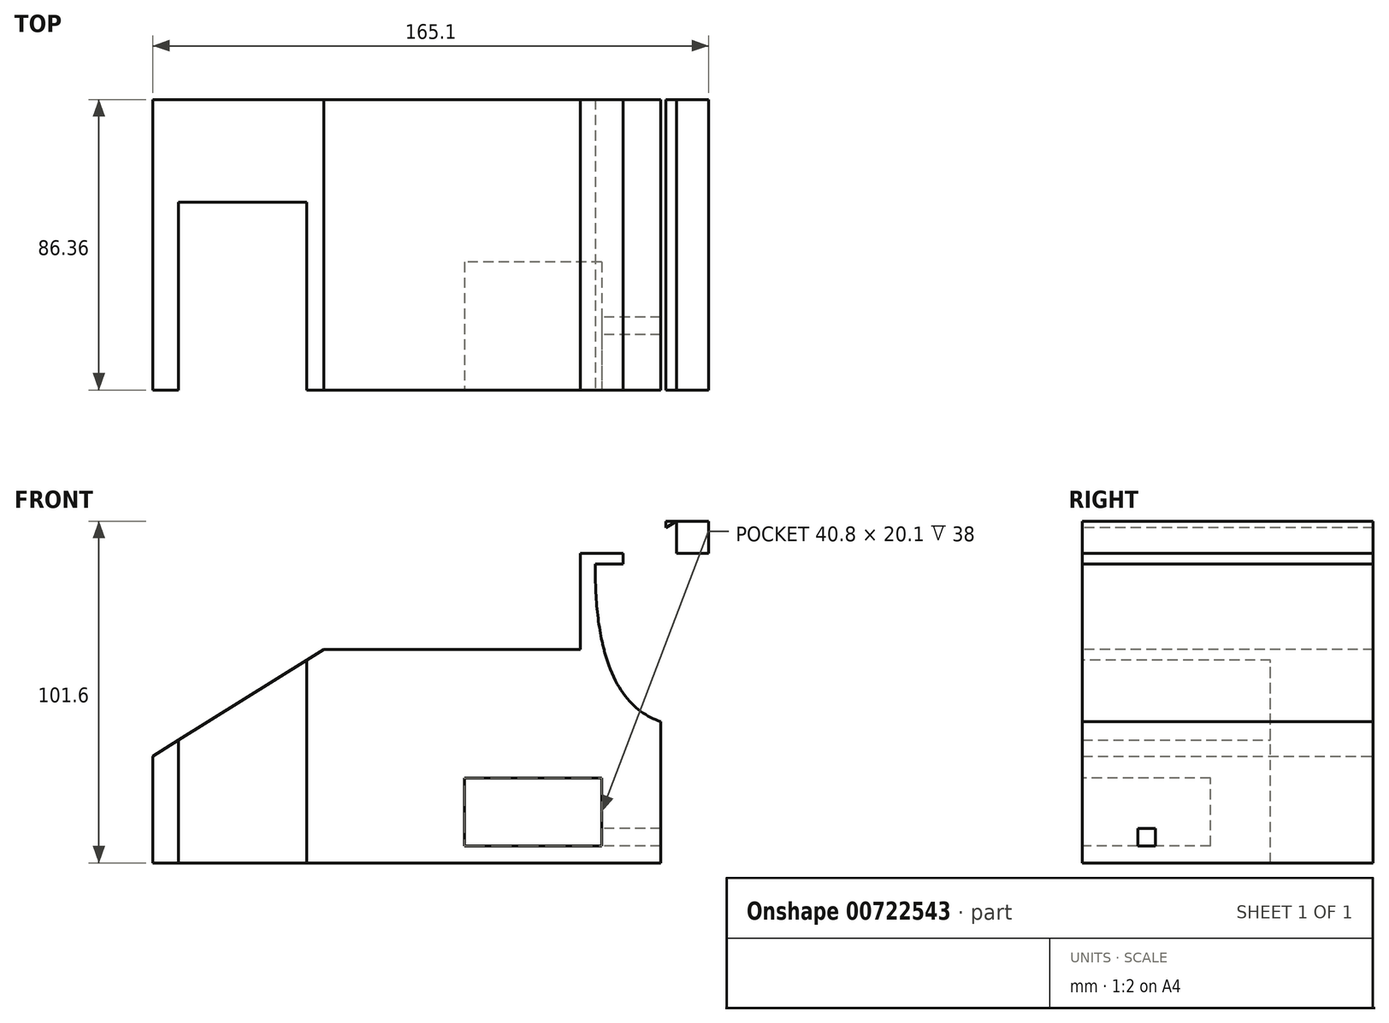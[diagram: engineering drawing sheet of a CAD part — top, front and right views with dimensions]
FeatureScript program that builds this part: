
annotation { "Feature Type Name" : "Feature", "Feature Type Description" : "" }
export const myFeature = defineFeature(function(context is Context, id is Id, definition is map)
    precondition{}
    {
        {
            var Q0;
            Q0=qCreatedBy(makeId("Top.planeOp"),FACE);
            var sketch = newSketch(context, id + "F0", { "sketchPlane" : qUnion([Q0])});
            skLineSegment(sketch, "E0.bottom", {"start": v(25.4, -38.7) * mm, "end": v(-25.4, -38.7) * mm});
            skLineSegment(sketch, "E0.top", {"start": v(25.4, 47.66) * mm, "end": v(-25.4, 47.66) * mm});
            skLineSegment(sketch, "E0.left", {"start": v(25.4, -38.7) * mm, "end": v(25.4, 47.66) * mm});
            skLineSegment(sketch, "E0.right", {"start": v(-25.4, -38.7) * mm, "end": v(-25.4, 47.66) * mm});
            skPoint(sketch, "E0.middle", {"position": v(0, 4.48) * mm});
            skSolve(sketch);
        }
        {
            var Q0;
            Q0=makeQuery(id+"F0.imprint","IMPRINT",FACE,{"disambiguationData":[TD([[makeQuery(id+"F0.imprint","IMPRINT",EDGE,{"derivedFrom":sQuery(id+"F0.wireOp",EDGE,"E0.bottom")}),-1.0]])]});
            extrude(context, id + "F1", {"entities" : qUnion([Q0]), "depth" : 63.5 * mm, "offsetDistance" : 25.4 * mm});
        }
        {
            var Q0;
            Q0=makeQuery(id+"F1.opExtrude","CAP_FACE",FACE,{"disambiguationData":[OSD([sQuery(id+"F0.wireOp",EDGE,"E0.bottom"),sQuery(id+"F0.wireOp",EDGE,"E0.top"),sQuery(id+"F0.wireOp",EDGE,"E0.left"),sQuery(id+"F0.wireOp",EDGE,"E0.right")])],"isStart":false});
            var sketch = newSketch(context, id + "F2", { "sketchPlane" : qUnion([Q0])});
            skLineSegment(sketch, "E1", {"start": v(0, 47.66) * mm, "end": v(0, -38.7) * mm});
            skLineSegment(sketch, "E2", {"start": v(-25.4, 4.48) * mm, "end": v(25.4, 4.48) * mm});
            skPoint(sketch, "E3.middle", {"position": v(0, 4.48) * mm});
            skLineSegment(sketch, "E4", {"start": v(-25.4, -38.7) * mm, "end": v(-17.78, -38.7) * mm});
            skLineSegment(sketch, "E5", {"start": v(25.4, -38.7) * mm, "end": v(20.32, -38.7) * mm});
            skLineSegment(sketch, "E6", {"start": v(20.32, -38.7) * mm, "end": v(20.32, 17.18) * mm});
            skLineSegment(sketch, "E7", {"start": v(20.32, 17.18) * mm, "end": v(-17.78, 17.18) * mm});
            skLineSegment(sketch, "E8", {"start": v(-17.78, 17.18) * mm, "end": v(-17.78, -38.7) * mm});
            skSolve(sketch);
        }
        {
            var Q0;
            {var subQ0=sQuery(id+"F2.wireOp",EDGE,"E1");var subQ1=makeQuery(id+"F1.opExtrude","CAP_EDGE",EDGE,{"disambiguationData":[OSD([sQuery(id+"F0.wireOp",EDGE,"E0.bottom")])],"isStart":false});var subQ2=makeQuery(id+"F2.imprint","INTERSECT",VERTEX,{"derivedFrom":[subQ1,subQ0]});Q0=makeQuery(id+"F2.imprint","IMPRINT",FACE,{"disambiguationData":[TD([[makeQuery(id+"F2.imprint","IMPRINT",EDGE,{"disambiguationData":[TD([[subQ2,1.0]])],"derivedFrom":subQ0}),1.0]])]});}
            var Q1;
            {var subQ0=sQuery(id+"F2.wireOp",EDGE,"E1");var subQ1=makeQuery(id+"F1.opExtrude","CAP_EDGE",EDGE,{"disambiguationData":[OSD([sQuery(id+"F0.wireOp",EDGE,"E0.bottom")])],"isStart":false});var subQ2=makeQuery(id+"F2.imprint","INTERSECT",VERTEX,{"derivedFrom":[subQ1,subQ0]});Q1=makeQuery(id+"F2.imprint","IMPRINT",FACE,{"disambiguationData":[TD([[makeQuery(id+"F2.imprint","IMPRINT",EDGE,{"disambiguationData":[TD([[subQ2,1.0]])],"derivedFrom":subQ0}),-1.0]])]});}
            var Q2;
            {var subQ0=sQuery(id+"F2.wireOp",EDGE,"E7");var subQ1=sQuery(id+"F2.wireOp",EDGE,"E1");var subQ2=makeQuery(id+"F2.imprint","INTERSECT",VERTEX,{"derivedFrom":[subQ1,subQ0]});Q2=makeQuery(id+"F2.imprint","IMPRINT",FACE,{"disambiguationData":[TD([[makeQuery(id+"F2.imprint","IMPRINT",EDGE,{"disambiguationData":[TD([[subQ2,-1.0]])],"derivedFrom":subQ1}),-1.0]])]});}
            var Q3;
            {var subQ0=sQuery(id+"F2.wireOp",EDGE,"E7");var subQ1=sQuery(id+"F2.wireOp",EDGE,"E1");var subQ2=makeQuery(id+"F2.imprint","INTERSECT",VERTEX,{"derivedFrom":[subQ1,subQ0]});Q3=makeQuery(id+"F2.imprint","IMPRINT",FACE,{"disambiguationData":[TD([[makeQuery(id+"F2.imprint","IMPRINT",EDGE,{"disambiguationData":[TD([[subQ2,-1.0]])],"derivedFrom":subQ1}),1.0]])]});}
            extrude(context, id + "F3", {"entities" : qUnion([Q0, Q1, Q2, Q3]), "operationType" : NewBodyOperationType.REMOVE, "oppositeDirection" : true, "depth" : 228.6 * mm, "offsetDistance" : 25.4 * mm});
        }
        {
            var Q0;
            Q0=makeQuery(id+"F1.opExtrude","SWEPT_FACE",FACE,{"disambiguationData":[OSD([sQuery(id+"F0.wireOp",EDGE,"E0.top")])]});
            var sketch = newSketch(context, id + "F4", { "sketchPlane" : qUnion([Q0])});
            skLineSegment(sketch, "E9", {"start": v(25.4, 0) * mm, "end": v(25.4, 31.75) * mm});
            skLineSegment(sketch, "E10", {"start": v(25.4, 31.75) * mm, "end": v(-25.4, 63.5) * mm});
            skSolve(sketch);
        }
        {
            var Q0;
            {var subQ0=sQuery(id+"F4.wireOp",EDGE,"E10");Q0=makeQuery(id+"F4.imprint","IMPRINT",FACE,{"disambiguationData":[TD([[makeQuery(id+"F4.imprint","IMPRINT",EDGE,{"derivedFrom":subQ0}),-1.0]])]});}
            extrude(context, id + "F5", {"entities" : qUnion([Q0]), "operationType" : NewBodyOperationType.REMOVE, "oppositeDirection" : true, "depth" : 228.6 * mm, "offsetDistance" : 25.4 * mm});
        }
        {
            var Q0;
            Q0=makeQuery(id+"F1.opExtrude","SWEPT_FACE",FACE,{"disambiguationData":[OSD([sQuery(id+"F0.wireOp",EDGE,"E0.left")])]});
            var sketch = newSketch(context, id + "F6", { "sketchPlane" : qUnion([Q0])});
            skLineSegment(sketch, "E11.bottom", {"start": v(-38.7, 0) * mm, "end": v(47.66, 0) * mm});
            skLineSegment(sketch, "E11.top", {"start": v(-38.7, 114.3) * mm, "end": v(47.66, 114.3) * mm});
            skLineSegment(sketch, "E11.left", {"start": v(-38.7, 0) * mm, "end": v(-38.7, 114.3) * mm});
            skLineSegment(sketch, "E11.right", {"start": v(47.66, 0) * mm, "end": v(47.66, 114.3) * mm});
            skSolve(sketch);
        }
        {
            var Q0;
            {var subQ0=sQuery(id+"F6.wireOp",EDGE,"E11.top");Q0=makeQuery(id+"F6.imprint","IMPRINT",FACE,{"disambiguationData":[TD([[makeQuery(id+"F6.imprint","IMPRINT",EDGE,{"derivedFrom":subQ0}),-1.0]])]});}
            var Q1;
            {var subQ0=sQuery(id+"F6.wireOp",EDGE,"E11.bottom");Q1=makeQuery(id+"F6.imprint","IMPRINT",FACE,{"disambiguationData":[TD([[makeQuery(id+"F6.imprint","IMPRINT",EDGE,{"derivedFrom":subQ0}),1.0]])]});}
            extrude(context, id + "F7", {"entities" : qUnion([Q0, Q1]), "operationType" : NewBodyOperationType.ADD, "depth" : 127 * mm, "offsetDistance" : 25.4 * mm});
        }
        {
            var Q0;
            {var subQ1=sQuery(id+"F0.wireOp",EDGE,"E0.left");var subQ3=sQuery(id+"F0.wireOp",EDGE,"E0.bottom");Q0=makeQuery(id+"F7.boolean.opBoolean","MERGE",FACE,{"derivedFrom":[makeQuery(id+"F3.boolean.opBoolean","SPLIT",FACE,{"disambiguationData":[TD([makeQuery(id+"F1.opExtrude","SWEPT_FACE",FACE,{"disambiguationData":[OSD([subQ1])]})])],"derivedFrom":makeQuery(id+"F1.opExtrude","SWEPT_FACE",FACE,{"disambiguationData":[OSD([subQ3])]})}),makeQuery(id+"F7.opExtrude","SWEPT_FACE",FACE,{"disambiguationData":[OSD([sQuery(id+"F6.wireOp",EDGE,"E11.left")])]})]});}
            var sketch = newSketch(context, id + "F8", { "sketchPlane" : qUnion([Q0])});
            skLineSegment(sketch, "E12", {"start": v(25.4, 63.5) * mm, "end": v(152.4, 63.5) * mm});
            skLineSegment(sketch, "E13", {"start": v(152.4, 114.3) * mm, "end": v(101.6, 114.3) * mm});
            skLineSegment(sketch, "E14", {"start": v(101.6, 114.3) * mm, "end": v(101.6, 63.5) * mm});
            skLineSegment(sketch, "E15", {"start": v(101.6, 63.5) * mm, "end": v(101.6, 88.9) * mm});
            skFitSpline(sketch, "E16", {"points": [v(101.6, 88.9) * mm, v(56.46, 63.5) * mm, v(25.4, 114.3) * mm, v(19.9, 130.64) * mm], "startDerivative": vector(-196.62, -34.97) * mm, "endDerivative": vector(-5.13, 63.21) * mm});
            skSolve(sketch);
        }
        {
            var Q0;
            {var subQ1=sQuery(id+"F0.wireOp",EDGE,"E0.left");var subQ3=sQuery(id+"F0.wireOp",EDGE,"E0.bottom");Q0=makeQuery(id+"F7.boolean.opBoolean","MERGE",FACE,{"derivedFrom":[makeQuery(id+"F3.boolean.opBoolean","SPLIT",FACE,{"disambiguationData":[TD([makeQuery(id+"F1.opExtrude","SWEPT_FACE",FACE,{"disambiguationData":[OSD([subQ1])]})])],"derivedFrom":makeQuery(id+"F1.opExtrude","SWEPT_FACE",FACE,{"disambiguationData":[OSD([subQ3])]})}),makeQuery(id+"F7.opExtrude","SWEPT_FACE",FACE,{"disambiguationData":[OSD([sQuery(id+"F6.wireOp",EDGE,"E11.left")])]})]});}
            var sketch = newSketch(context, id + "F9", { "sketchPlane" : qUnion([Q0])});
            skLineSegment(sketch, "E17", {"start": v(25.4, 63.5) * mm, "end": v(152.4, 63.5) * mm});
            skSolve(sketch);
        }
        {
            var Q0;
            Q0=qSketchRegion(id+"F9",true);
            var Q1;
            {var subQ1=sQuery(id+"F6.wireOp",EDGE,"E11.left");var subQ2=makeQuery(id+"F7.opExtrude","CAP_EDGE",EDGE,{"disambiguationData":[OSD([subQ1])],"isStart":true});Q1=makeQuery(id+"F9.imprint","IMPRINT",FACE,{"disambiguationData":[TD([[makeQuery(id+"F9.imprint","IMPRINT",EDGE,{"derivedFrom":subQ2}),-1.0]])]});}
            extrude(context, id + "F10", {"entities" : qUnion([Q0, Q1]), "operationType" : NewBodyOperationType.REMOVE, "oppositeDirection" : true, "depth" : 228.6 * mm, "offsetDistance" : 25.4 * mm});
        }
        {
            var Q0;
            {var subQ1=sQuery(id+"F0.wireOp",EDGE,"E0.left");var subQ3=sQuery(id+"F0.wireOp",EDGE,"E0.bottom");Q0=makeQuery(id+"F7.boolean.opBoolean","MERGE",FACE,{"derivedFrom":[makeQuery(id+"F3.boolean.opBoolean","SPLIT",FACE,{"disambiguationData":[TD([makeQuery(id+"F1.opExtrude","SWEPT_FACE",FACE,{"disambiguationData":[OSD([subQ1])]})])],"derivedFrom":makeQuery(id+"F1.opExtrude","SWEPT_FACE",FACE,{"disambiguationData":[OSD([subQ3])]})}),makeQuery(id+"F7.opExtrude","SWEPT_FACE",FACE,{"disambiguationData":[OSD([sQuery(id+"F6.wireOp",EDGE,"E11.left")])]})]});}
            var sketch = newSketch(context, id + "F11", { "sketchPlane" : qUnion([Q0])});
            skLineSegment(sketch, "E18", {"start": v(152.4, 13.36) * mm, "end": v(107.95, 13.36) * mm});
            skLineSegment(sketch, "E19", {"start": v(107.95, 5.08) * mm, "end": v(107.95, 13.36) * mm});
            skLineSegment(sketch, "E20", {"start": v(107.95, 5.08) * mm, "end": v(67.15, 5.08) * mm});
            skLineSegment(sketch, "E21", {"start": v(67.15, 5.08) * mm, "end": v(67.15, 25.18) * mm});
            skLineSegment(sketch, "E22", {"start": v(67.15, 25.18) * mm, "end": v(107.95, 25.18) * mm});
            skLineSegment(sketch, "E23", {"start": v(107.95, 25.18) * mm, "end": v(107.95, 5.08) * mm});
            skSolve(sketch);
        }
        {
            var Q0;
            {var subQ1=sQuery(id+"F11.wireOp",EDGE,"E21");Q0=makeQuery(id+"F11.imprint","IMPRINT",FACE,{"disambiguationData":[TD([[makeQuery(id+"F11.imprint","IMPRINT",EDGE,{"derivedFrom":subQ1}),-1.0]])]});}
            extrude(context, id + "F12", {"entities" : qUnion([Q0]), "operationType" : NewBodyOperationType.REMOVE, "oppositeDirection" : true, "depth" : 38 * mm, "offsetDistance" : 25.4 * mm});
        }
        {
            var Q0;
            {var subQ0=sQuery(id+"F8.wireOp",EDGE,"E15");Q0=makeQuery(id+"F8.imprint","IMPRINT",FACE,{"disambiguationData":[TD([[makeQuery(id+"F8.imprint","IMPRINT",EDGE,{"derivedFrom":subQ0}),1.0]])]});}
            var Q1;
            {var subQ1=sQuery(id+"F8.wireOp",EDGE,"E13");Q1=makeQuery(id+"F8.imprint","IMPRINT",FACE,{"disambiguationData":[TD([[makeQuery(id+"F8.imprint","IMPRINT",EDGE,{"derivedFrom":subQ1}),1.0]])]});}
            extrude(context, id + "F13", {"entities" : qUnion([Q0, Q1]), "operationType" : NewBodyOperationType.ADD, "oppositeDirection" : true, "depth" : 86.36 * mm, "offsetDistance" : 25.4 * mm});
        }
        {
            var Q0;
            {var subQ0=sQuery(id+"F6.wireOp",EDGE,"E11.left");Q0=makeQuery(id+"F13.boolean.opBoolean","MERGE",FACE,{"derivedFrom":[makeQuery(id+"F7.opExtrude","CAP_FACE",FACE,{"disambiguationData":[OSD([sQuery(id+"F6.wireOp",EDGE,"E11.bottom"),sQuery(id+"F6.wireOp",EDGE,"E11.top"),subQ0,sQuery(id+"F6.wireOp",EDGE,"E11.right")])],"isStart":false}),makeQuery(id+"F13.opExtrude","SWEPT_FACE",FACE,{"disambiguationData":[OSD([subQ0])]})]});}
            var sketch = newSketch(context, id + "F14", { "sketchPlane" : qUnion([Q0])});
            skLineSegment(sketch, "E24", {"start": v(-38.7, 114.3) * mm, "end": v(-38.7, 88.9) * mm});
            skLineSegment(sketch, "E25", {"start": v(-38.7, 88.9) * mm, "end": v(47.66, 88.9) * mm});
            skLineSegment(sketch, "E26", {"start": v(47.66, 88.9) * mm, "end": v(47.66, 101.6) * mm});
            skSolve(sketch);
        }
        {
            var Q0;
            Q0=makeQuery(id+"F14.imprint","IMPRINT",FACE,{"disambiguationData":[TD([[makeQuery(id+"F14.imprint","IMPRINT",EDGE,{"derivedFrom":sQuery(id+"F14.wireOp",EDGE,"E24")}),-1.0]])]});
            extrude(context, id + "F15", {"entities" : qUnion([Q0]), "operationType" : NewBodyOperationType.REMOVE, "oppositeDirection" : true, "depth" : 101.6 * mm, "offsetDistance" : 25.4 * mm});
        }
        {
            var Q0;
            {var subQ0=sQuery(id+"F6.wireOp",EDGE,"E11.left");var subQ2=sQuery(id+"F0.wireOp",EDGE,"E0.left");var subQ4=sQuery(id+"F0.wireOp",EDGE,"E0.bottom");Q0=makeQuery(id+"F13.boolean.opBoolean","MERGE",FACE,{"derivedFrom":[makeQuery(id+"F7.boolean.opBoolean","MERGE",FACE,{"derivedFrom":[makeQuery(id+"F3.boolean.opBoolean","SPLIT",FACE,{"disambiguationData":[TD([makeQuery(id+"F1.opExtrude","SWEPT_FACE",FACE,{"disambiguationData":[OSD([subQ2])]})])],"derivedFrom":makeQuery(id+"F1.opExtrude","SWEPT_FACE",FACE,{"disambiguationData":[OSD([subQ4])]})}),makeQuery(id+"F7.opExtrude","SWEPT_FACE",FACE,{"disambiguationData":[OSD([subQ0])]})]}),makeQuery(id+"F13.opExtrude","CAP_FACE",FACE,{"disambiguationData":[OSD([subQ0,sQuery(id+"F8.wireOp",EDGE,"E12"),sQuery(id+"F8.wireOp",EDGE,"E13"),sQuery(id+"F8.wireOp",EDGE,"E14"),sQuery(id+"F8.wireOp",EDGE,"E16")])],"isStart":true})]});}
            var sketch = newSketch(context, id + "F16", { "sketchPlane" : qUnion([Q0])});
            skLineSegment(sketch, "E27", {"start": v(101.6, 88.9) * mm, "end": v(101.6, 0) * mm});
            skLineSegment(sketch, "E28", {"start": v(101.6, 0) * mm, "end": v(101.6, 44.45) * mm});
            skLineSegment(sketch, "E29", {"start": v(101.6, 44.45) * mm, "end": v(101.6, 88.9) * mm});
            skLineSegment(sketch, "E30", {"start": v(101.6, 66.68) * mm, "end": v(152.4, 66.68) * mm});
            skLineSegment(sketch, "E31", {"start": v(101.6, 88.9) * mm, "end": v(110.49, 88.9) * mm});
            skLineSegment(sketch, "E32", {"start": v(110.49, 88.9) * mm, "end": v(110.49, 0) * mm});
            skLineSegment(sketch, "E33", {"start": v(125.47, 45.06) * mm, "end": v(125.47, 0) * mm});
            skFitSpline(sketch, "E34", {"points": [v(106.04, 88.9) * mm, v(152.4, 44.45) * mm, v(157.72, 45.76) * mm], "startDerivative": vector(-2.32, -246.99) * mm, "endDerivative": vector(30.68, 18.7) * mm});
            skSolve(sketch);
        }
        {
            var Q0;
            {var subQ0=sQuery(id+"F16.wireOp",EDGE,"E34");var subQ1=sQuery(id+"F16.wireOp",EDGE,"E30");var subQ2=makeQuery(id+"F16.imprint","INTERSECT",VERTEX,{"derivedFrom":[subQ1,subQ0]});Q0=makeQuery(id+"F16.imprint","IMPRINT",FACE,{"disambiguationData":[TD([[makeQuery(id+"F16.imprint","IMPRINT",EDGE,{"disambiguationData":[TD([[subQ2,-1.0]])],"derivedFrom":subQ1}),1.0]])]});}
            var Q1;
            {var subQ0=sQuery(id+"F16.wireOp",EDGE,"E30");var subQ4=sQuery(id+"F16.wireOp",EDGE,"E32");var subQ5=makeQuery(id+"F16.imprint","INTERSECT",VERTEX,{"derivedFrom":[subQ0,subQ4]});Q1=makeQuery(id+"F16.imprint","IMPRINT",FACE,{"disambiguationData":[TD([[makeQuery(id+"F16.imprint","IMPRINT",EDGE,{"disambiguationData":[TD([[subQ5,-1.0]])],"derivedFrom":subQ0}),1.0]])]});}
            var Q2;
            {var subQ0=sQuery(id+"F16.wireOp",EDGE,"E33");var subQ6=sQuery(id+"F16.wireOp",EDGE,"E34");var subQ7=makeQuery(id+"F16.imprint","INTERSECT",VERTEX,{"derivedFrom":[subQ0,subQ6]});Q2=makeQuery(id+"F16.imprint","IMPRINT",FACE,{"disambiguationData":[TD([[makeQuery(id+"F16.imprint","IMPRINT",EDGE,{"disambiguationData":[TD([[subQ7,-1.0]])],"derivedFrom":subQ6}),-1.0]])]});}
            var Q3;
            {var subQ2=sQuery(id+"F16.wireOp",EDGE,"E32");var subQ4=sQuery(id+"F16.wireOp",EDGE,"E30");var subQ5=makeQuery(id+"F16.imprint","INTERSECT",VERTEX,{"derivedFrom":[subQ4,subQ2]});Q3=makeQuery(id+"F16.imprint","IMPRINT",FACE,{"disambiguationData":[TD([[makeQuery(id+"F16.imprint","IMPRINT",EDGE,{"disambiguationData":[TD([[subQ5,-1.0]])],"derivedFrom":subQ2}),1.0]])]});}
            var Q4;
            {var subQ0=sQuery(id+"F16.wireOp",EDGE,"E34");var subQ1=sQuery(id+"F16.wireOp",EDGE,"E30");var subQ2=makeQuery(id+"F16.imprint","INTERSECT",VERTEX,{"derivedFrom":[subQ1,subQ0]});Q4=makeQuery(id+"F16.imprint","IMPRINT",FACE,{"disambiguationData":[TD([[makeQuery(id+"F16.imprint","IMPRINT",EDGE,{"disambiguationData":[TD([[subQ2,-1.0]])],"derivedFrom":subQ1}),-1.0]])]});}
            extrude(context, id + "F17", {"entities" : qUnion([Q0, Q1, Q2, Q3, Q4]), "operationType" : NewBodyOperationType.REMOVE, "oppositeDirection" : true, "depth" : 228.6 * mm, "offsetDistance" : 25.4 * mm});
        }
        {
            var Q0;
            Q0=makeQuery(id+"F15.boolean.opBoolean","COPY",FACE,{"derivedFrom":makeQuery(id+"F15.opExtrude","SWEPT_FACE",FACE,{"disambiguationData":[OSD([sQuery(id+"F14.wireOp",EDGE,"E25")])]})});
            var sketch = newSketch(context, id + "F18", { "sketchPlane" : qUnion([Q0])});
            skLineSegment(sketch, "E35.bottom", {"start": v(101.6, 47.66) * mm, "end": v(152.4, 47.66) * mm});
            skLineSegment(sketch, "E35.top", {"start": v(101.6, -38.7) * mm, "end": v(152.4, -38.7) * mm});
            skLineSegment(sketch, "E35.left", {"start": v(101.6, 47.66) * mm, "end": v(101.6, -38.7) * mm});
            skLineSegment(sketch, "E35.right", {"start": v(152.4, 47.66) * mm, "end": v(152.4, -38.7) * mm});
            skSolve(sketch);
        }
        {
            var Q0;
            {var subQ2=sQuery(id+"F18.wireOp",EDGE,"E35.right");Q0=makeQuery(id+"F18.imprint","IMPRINT",FACE,{"disambiguationData":[TD([[makeQuery(id+"F18.imprint","IMPRINT",EDGE,{"derivedFrom":subQ2}),-1.0]])]});}
            var Q1;
            {var subQ0=sQuery(id+"F18.wireOp",EDGE,"E35.left");Q1=makeQuery(id+"F18.imprint","IMPRINT",FACE,{"disambiguationData":[TD([[makeQuery(id+"F18.imprint","IMPRINT",EDGE,{"derivedFrom":subQ0}),1.0]])]});}
            extrude(context, id + "F19", {"entities" : qUnion([Q0, Q1]), "operationType" : NewBodyOperationType.ADD, "depth" : 12.7 * mm, "offsetDistance" : 25.4 * mm});
        }
        {
            var Q0;
            {var subQ0=sQuery(id+"F6.wireOp",EDGE,"E11.left");var subQ2=sQuery(id+"F0.wireOp",EDGE,"E0.left");var subQ4=sQuery(id+"F0.wireOp",EDGE,"E0.bottom");Q0=makeQuery(id+"F19.boolean.opBoolean","MERGE",FACE,{"derivedFrom":[makeQuery(id+"F13.boolean.opBoolean","MERGE",FACE,{"derivedFrom":[makeQuery(id+"F7.boolean.opBoolean","MERGE",FACE,{"derivedFrom":[makeQuery(id+"F3.boolean.opBoolean","SPLIT",FACE,{"disambiguationData":[TD([makeQuery(id+"F1.opExtrude","SWEPT_FACE",FACE,{"disambiguationData":[OSD([subQ2])]})])],"derivedFrom":makeQuery(id+"F1.opExtrude","SWEPT_FACE",FACE,{"disambiguationData":[OSD([subQ4])]})}),makeQuery(id+"F7.opExtrude","SWEPT_FACE",FACE,{"disambiguationData":[OSD([subQ0])]})]}),makeQuery(id+"F13.opExtrude","CAP_FACE",FACE,{"disambiguationData":[OSD([subQ0,sQuery(id+"F8.wireOp",EDGE,"E12"),sQuery(id+"F8.wireOp",EDGE,"E13"),sQuery(id+"F8.wireOp",EDGE,"E14"),sQuery(id+"F8.wireOp",EDGE,"E16")])],"isStart":true})]}),makeQuery(id+"F19.opExtrude","SWEPT_FACE",FACE,{"disambiguationData":[OSD([sQuery(id+"F18.wireOp",EDGE,"E35.top")])]})]});}
            var sketch = newSketch(context, id + "F20", { "sketchPlane" : qUnion([Q0])});
            skLineSegment(sketch, "E36", {"start": v(152.4, 101.6) * mm, "end": v(152.4, 88.9) * mm});
            skLineSegment(sketch, "E37", {"start": v(152.4, 88.9) * mm, "end": v(152.4, 95.25) * mm});
            skLineSegment(sketch, "E38", {"start": v(152.4, 95.25) * mm, "end": v(152.4, 92.08) * mm});
            skLineSegment(sketch, "E39", {"start": v(152.4, 92.08) * mm, "end": v(101.6, 92.08) * mm});
            skLineSegment(sketch, "E40", {"start": v(127, 101.6) * mm, "end": v(127, 88.9) * mm});
            skPoint(sketch, "E40.endSnap0", {"position": v(127, 92.08) * mm});
            skLineSegment(sketch, "E41", {"start": v(101.6, 101.6) * mm, "end": v(127, 101.6) * mm});
            skLineSegment(sketch, "E42", {"start": v(114.3, 101.6) * mm, "end": v(114.3, 88.9) * mm});
            skLineSegment(sketch, "E43", {"start": v(152.4, 101.6) * mm, "end": v(127, 101.6) * mm});
            skLineSegment(sketch, "E44", {"start": v(139.7, 101.6) * mm, "end": v(139.7, 88.9) * mm});
            skLineSegment(sketch, "E45", {"start": v(139.7, 88.9) * mm, "end": v(139.7, 101.6) * mm});
            skLineSegment(sketch, "E46", {"start": v(127, 101.6) * mm, "end": v(139.7, 101.6) * mm});
            skLineSegment(sketch, "E47", {"start": v(133.35, 101.6) * mm, "end": v(133.35, 88.9) * mm});
            skLineSegment(sketch, "E48", {"start": v(133.35, 88.9) * mm, "end": v(133.35, 101.6) * mm});
            skLineSegment(sketch, "E49", {"start": v(127, 101.6) * mm, "end": v(133.35, 101.6) * mm});
            skLineSegment(sketch, "E50", {"start": v(130.17, 101.6) * mm, "end": v(130.17, 88.9) * mm});
            skLineSegment(sketch, "E51", {"start": v(130.17, 101.6) * mm, "end": v(114.3, 101.6) * mm});
            skLineSegment(sketch, "E52", {"start": v(114.3, 92.08) * mm, "end": v(130.17, 101.6) * mm});
            skSolve(sketch);
        }
        {
            var Q0;
            {var subQ5=sQuery(id+"F20.wireOp",EDGE,"E41");Q0=makeQuery(id+"F20.imprint","IMPRINT",FACE,{"disambiguationData":[TD([[makeQuery(id+"F20.imprint","IMPRINT",EDGE,{"derivedFrom":subQ5}),-1.0]])]});}
            var Q1;
            {var subQ0=sQuery(id+"F20.wireOp",EDGE,"E51");var subQ1=sQuery(id+"F20.wireOp",EDGE,"E40");var subQ2=makeQuery(id+"F20.imprint","INTERSECT",VERTEX,{"derivedFrom":[subQ1,subQ0]});Q1=makeQuery(id+"F20.imprint","IMPRINT",FACE,{"disambiguationData":[TD([[makeQuery(id+"F20.imprint","IMPRINT",EDGE,{"disambiguationData":[TD([[subQ2,-1.0]])],"derivedFrom":subQ1}),-1.0]])]});}
            var Q2;
            {var subQ0=sQuery(id+"F20.wireOp",EDGE,"E51");var subQ1=sQuery(id+"F20.wireOp",EDGE,"E40");var subQ2=makeQuery(id+"F20.imprint","INTERSECT",VERTEX,{"derivedFrom":[subQ1,subQ0]});Q2=makeQuery(id+"F20.imprint","IMPRINT",FACE,{"disambiguationData":[TD([[makeQuery(id+"F20.imprint","IMPRINT",EDGE,{"disambiguationData":[TD([[subQ2,-1.0]])],"derivedFrom":subQ1}),1.0]])]});}
            var Q3;
            {var subQ5=sQuery(id+"F20.wireOp",EDGE,"E49");Q3=makeQuery(id+"F20.imprint","IMPRINT",FACE,{"disambiguationData":[TD([[makeQuery(id+"F20.imprint","IMPRINT",EDGE,{"derivedFrom":subQ5}),-1.0]])]});}
            var Q4;
            {var subQ5=sQuery(id+"F20.wireOp",EDGE,"E46");Q4=makeQuery(id+"F20.imprint","IMPRINT",FACE,{"disambiguationData":[TD([[makeQuery(id+"F20.imprint","IMPRINT",EDGE,{"derivedFrom":subQ5}),-1.0]])]});}
            var Q5;
            {var subQ0=sQuery(id+"F20.wireOp",EDGE,"E48");var subQ1=sQuery(id+"F20.wireOp",EDGE,"E39");var subQ2=makeQuery(id+"F20.imprint","INTERSECT",VERTEX,{"derivedFrom":[subQ1,subQ0]});Q5=makeQuery(id+"F20.imprint","IMPRINT",FACE,{"disambiguationData":[TD([[makeQuery(id+"F20.imprint","IMPRINT",EDGE,{"disambiguationData":[TD([[subQ2,-1.0]])],"derivedFrom":subQ1}),1.0]])]});}
            var Q6;
            {var subQ0=sQuery(id+"F20.wireOp",EDGE,"E45");var subQ1=sQuery(id+"F20.wireOp",EDGE,"E39");var subQ2=makeQuery(id+"F20.imprint","INTERSECT",VERTEX,{"derivedFrom":[subQ1,subQ0]});Q6=makeQuery(id+"F20.imprint","IMPRINT",FACE,{"disambiguationData":[TD([[makeQuery(id+"F20.imprint","IMPRINT",EDGE,{"disambiguationData":[TD([[subQ2,-1.0]])],"derivedFrom":subQ1}),1.0]])]});}
            var Q7;
            Q7=makeQuery(id+"F20.imprint","IMPRINT",FACE,{"disambiguationData":[TD([[makeQuery(id+"F20.imprint","IMPRINT",EDGE,{"derivedFrom":sQuery(id+"F20.wireOp",EDGE,"E36")}),-1.0]])]});
            var Q8;
            {var subQ0=sQuery(id+"F20.wireOp",EDGE,"E37");Q8=makeQuery(id+"F20.imprint","IMPRINT",FACE,{"disambiguationData":[TD([[makeQuery(id+"F20.imprint","IMPRINT",EDGE,{"derivedFrom":subQ0}),-1.0]])]});}
            extrude(context, id + "F21", {"entities" : qUnion([Q0, Q1, Q2, Q3, Q4, Q5, Q6, Q7, Q8]), "operationType" : NewBodyOperationType.REMOVE, "oppositeDirection" : true, "depth" : 228.6 * mm, "offsetDistance" : 25.4 * mm});
        }
        {
            var Q0;
            {var subQ0=sQuery(id+"F6.wireOp",EDGE,"E11.left");var subQ2=sQuery(id+"F0.wireOp",EDGE,"E0.left");var subQ4=sQuery(id+"F0.wireOp",EDGE,"E0.bottom");Q0=makeQuery(id+"F19.boolean.opBoolean","MERGE",FACE,{"derivedFrom":[makeQuery(id+"F13.boolean.opBoolean","MERGE",FACE,{"derivedFrom":[makeQuery(id+"F7.boolean.opBoolean","MERGE",FACE,{"derivedFrom":[makeQuery(id+"F3.boolean.opBoolean","SPLIT",FACE,{"disambiguationData":[TD([makeQuery(id+"F1.opExtrude","SWEPT_FACE",FACE,{"disambiguationData":[OSD([subQ2])]})])],"derivedFrom":makeQuery(id+"F1.opExtrude","SWEPT_FACE",FACE,{"disambiguationData":[OSD([subQ4])]})}),makeQuery(id+"F7.opExtrude","SWEPT_FACE",FACE,{"disambiguationData":[OSD([subQ0])]})]}),makeQuery(id+"F13.opExtrude","CAP_FACE",FACE,{"disambiguationData":[OSD([subQ0,sQuery(id+"F8.wireOp",EDGE,"E12"),sQuery(id+"F8.wireOp",EDGE,"E13"),sQuery(id+"F8.wireOp",EDGE,"E14"),sQuery(id+"F8.wireOp",EDGE,"E16")])],"isStart":true})]}),makeQuery(id+"F19.opExtrude","SWEPT_FACE",FACE,{"disambiguationData":[OSD([sQuery(id+"F18.wireOp",EDGE,"E35.top")])]})]});}
            var sketch = newSketch(context, id + "F22", { "sketchPlane" : qUnion([Q0])});
            skLineSegment(sketch, "E53", {"start": v(114.3, 92.08) * mm, "end": v(114.3, 88.9) * mm});
            skLineSegment(sketch, "E54", {"start": v(114.3, 88.9) * mm, "end": v(130.17, 88.9) * mm});
            skLineSegment(sketch, "E55", {"start": v(130.17, 88.9) * mm, "end": v(130.17, 101.6) * mm});
            skLineSegment(sketch, "E56", {"start": v(130.17, 101.6) * mm, "end": v(130.17, 92.08) * mm});
            skLineSegment(sketch, "E57", {"start": v(130.17, 92.08) * mm, "end": v(114.3, 92.08) * mm});
            skLineSegment(sketch, "E58", {"start": v(122.24, 92.08) * mm, "end": v(130.17, 88.9) * mm});
            skLineSegment(sketch, "E59", {"start": v(122.24, 92.08) * mm, "end": v(114.3, 88.9) * mm});
            skSolve(sketch);
        }
        {
            var Q0;
            Q0=makeQuery(id+"F22.imprint","IMPRINT",FACE,{"disambiguationData":[TD([[makeQuery(id+"F22.imprint","IMPRINT",EDGE,{"derivedFrom":sQuery(id+"F22.wireOp",EDGE,"E54")}),1.0]])]});
            extrude(context, id + "F23", {"entities" : qUnion([Q0]), "operationType" : NewBodyOperationType.REMOVE, "oppositeDirection" : true, "depth" : 228.6 * mm, "offsetDistance" : 25.4 * mm});
        }
        {
            var Q0;
            Q0=makeQuery(id+"F12.boolean.opBoolean","COPY",FACE,{"derivedFrom":makeQuery(id+"F12.opExtrude","SWEPT_FACE",FACE,{"disambiguationData":[OSD([sQuery(id+"F11.wireOp",EDGE,"E23")])]})});
            var sketch = newSketch(context, id + "F24", { "sketchPlane" : qUnion([Q0])});
            skLineSegment(sketch, "E60.bottom", {"start": v(38.7, 25.18) * mm, "end": v(0.7, 25.18) * mm});
            skLineSegment(sketch, "E60.top", {"start": v(38.7, 5.08) * mm, "end": v(0.7, 5.08) * mm});
            skLineSegment(sketch, "E60.left", {"start": v(38.7, 25.18) * mm, "end": v(38.7, 5.08) * mm});
            skLineSegment(sketch, "E60.right", {"start": v(0.7, 25.18) * mm, "end": v(0.7, 5.08) * mm});
            skLineSegment(sketch, "E61", {"start": v(0.7, 5.08) * mm, "end": v(19.7, 5.08) * mm});
            skLineSegment(sketch, "E62", {"start": v(19.7, 5.08) * mm, "end": v(38.7, 5.08) * mm});
            skLineSegment(sketch, "E63", {"start": v(29.2, 5.08) * mm, "end": v(38.7, 5.08) * mm});
            skLineSegment(sketch, "E64", {"start": v(0.7, 5.08) * mm, "end": v(10.2, 5.08) * mm});
            skLineSegment(sketch, "E65", {"start": v(10.2, 5.08) * mm, "end": v(19.7, 5.08) * mm});
            skLineSegment(sketch, "E66", {"start": v(14.95, 5.08) * mm, "end": v(19.7, 5.08) * mm});
            skLineSegment(sketch, "E67", {"start": v(19.7, 5.08) * mm, "end": v(29.2, 5.08) * mm});
            skLineSegment(sketch, "E68", {"start": v(24.45, 5.08) * mm, "end": v(19.7, 5.08) * mm});
            skLineSegment(sketch, "E69", {"start": v(19.7, 5.08) * mm, "end": v(17.32, 5.08) * mm});
            skLineSegment(sketch, "E70", {"start": v(17.32, 5.08) * mm, "end": v(19.7, 5.08) * mm});
            skLineSegment(sketch, "E71", {"start": v(19.7, 5.08) * mm, "end": v(22.07, 5.08) * mm});
            skPoint(sketch, "E72.middle", {"position": v(19.7, 5.08) * mm});
            skLineSegment(sketch, "E73", {"start": v(19.7, 5.08) * mm, "end": v(22.3, 5.08) * mm});
            skLineSegment(sketch, "E74", {"start": v(22.3, 5.08) * mm, "end": v(17.1, 5.08) * mm});
            skLineSegment(sketch, "E75", {"start": v(22.3, 5.08) * mm, "end": v(22.3, 10.28) * mm});
            skLineSegment(sketch, "E76", {"start": v(17.1, 5.08) * mm, "end": v(17.1, 10.28) * mm});
            skLineSegment(sketch, "E77", {"start": v(17.1, 10.28) * mm, "end": v(22.3, 10.28) * mm});
            skSolve(sketch);
        }
        {
            var Q0;
            {var subQ0=sQuery(id+"F24.wireOp",EDGE,"E75");Q0=makeQuery(id+"F24.imprint","IMPRINT",FACE,{"disambiguationData":[TD([[makeQuery(id+"F24.imprint","IMPRINT",EDGE,{"derivedFrom":subQ0}),1.0]])]});}
            extrude(context, id + "F25", {"entities" : qUnion([Q0]), "operationType" : NewBodyOperationType.REMOVE, "oppositeDirection" : true, "depth" : 59.69 * mm, "offsetDistance" : 25.4 * mm});
        }
    });
